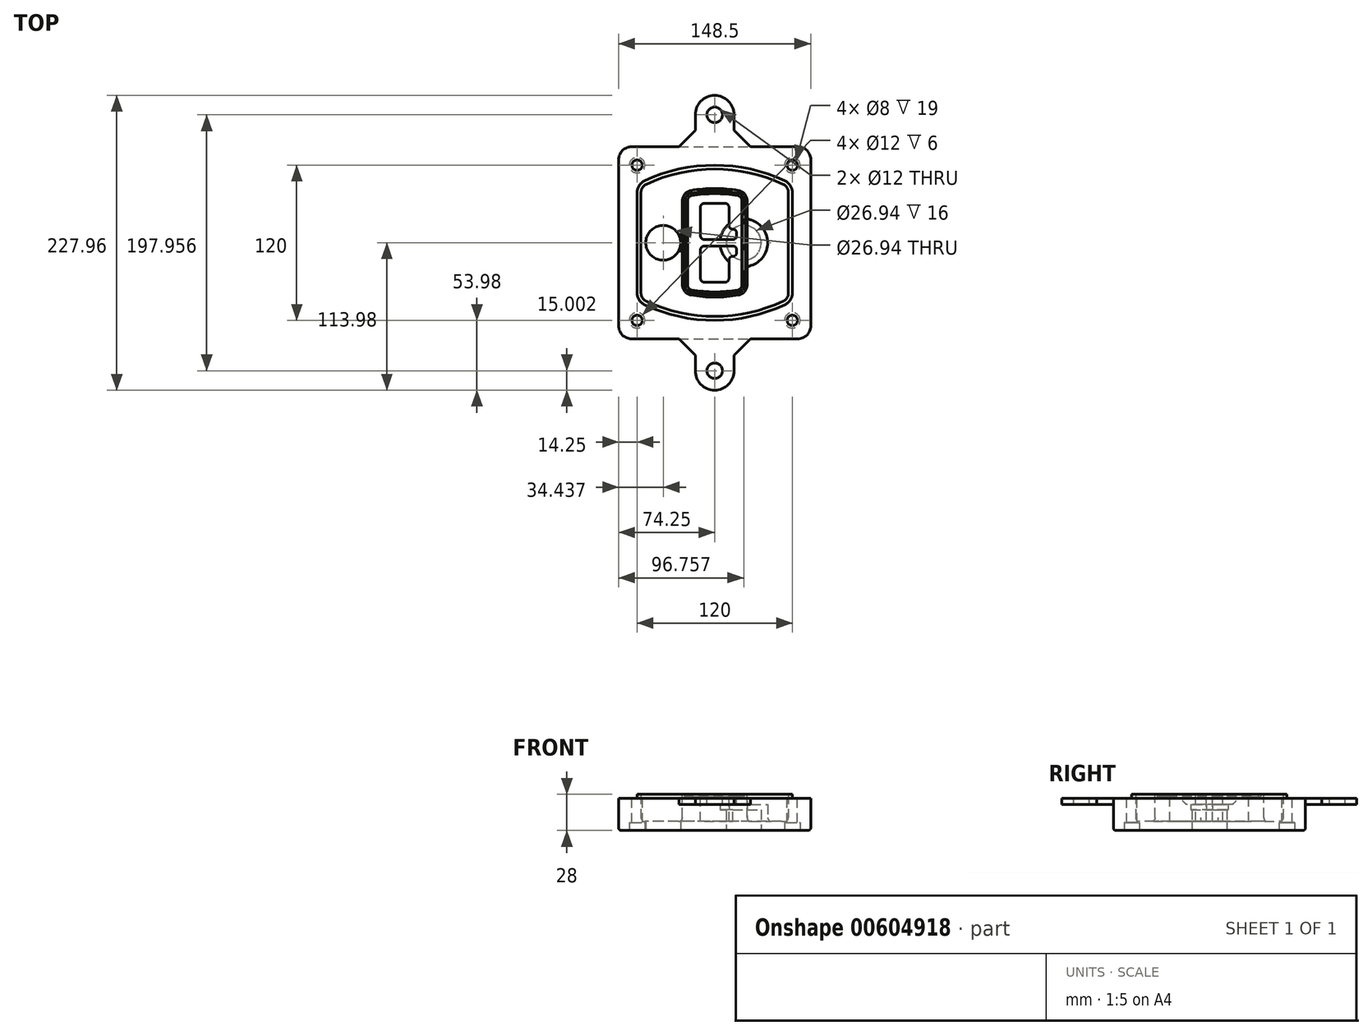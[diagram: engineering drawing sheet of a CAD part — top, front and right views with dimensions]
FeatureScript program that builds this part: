
annotation { "Feature Type Name" : "Feature", "Feature Type Description" : "" }
export const myFeature = defineFeature(function(context is Context, id is Id, definition is map)
    precondition{}
    {
        {
            var Q0;
            Q0=qCreatedBy(makeId("Top.planeOp"),FACE);
            var sketch = newSketch(context, id + "F0", { "sketchPlane" : qUnion([Q0])});
            skPoint(sketch, "E0.rect.middle", {"position": v(0, 0) * mm});
            skLineSegment(sketch, "E1.bottom", {"start": v(-64.25, -74.25) * mm, "end": v(64.25, -74.25) * mm});
            skLineSegment(sketch, "E1.top", {"start": v(-64.25, 74.25) * mm, "end": v(64.25, 74.25) * mm});
            skLineSegment(sketch, "E1.left", {"start": v(-74.25, -64.25) * mm, "end": v(-74.25, 64.25) * mm});
            skLineSegment(sketch, "E1.right", {"start": v(74.25, -64.25) * mm, "end": v(74.25, 64.25) * mm});
            skLineSegment(sketch, "E2", {"start": v(-74.25, 74.25) * mm, "end": v(74.25, -74.25) * mm, "construction": true});
            skLineSegment(sketch, "E3", {"start": v(74.25, 74.25) * mm, "end": v(-74.25, -74.25) * mm, "construction": true});
            skCircle(sketch, "E4", {"center": v(-60, 60) * mm, "radius": 4 * mm});
            skCircle(sketch, "E5", {"center": v(60, 60) * mm, "radius": 4 * mm});
            skCircle(sketch, "E6", {"center": v(60, -60) * mm, "radius": 4 * mm});
            skCircle(sketch, "E7", {"center": v(-60, -60) * mm, "radius": 4 * mm});
            skLineSegment(sketch, "E8", {"start": v(-60, 60) * mm, "end": v(60, 60) * mm, "construction": true});
            skLineSegment(sketch, "E9", {"start": v(60, 60) * mm, "end": v(60, -60) * mm, "construction": true});
            skLineSegment(sketch, "E10", {"start": v(60, -60) * mm, "end": v(-60, -60) * mm, "construction": true});
            skLineSegment(sketch, "E11", {"start": v(-60, -60) * mm, "end": v(-60, 60) * mm, "construction": true});
            skLineSegment(sketch, "E12", {"start": v(-60, 38.83) * mm, "end": v(-60, -38.83) * mm});
            skLineSegment(sketch, "E13", {"start": v(60, 38.83) * mm, "end": v(60, -38.83) * mm});
            skArc(sketch, "E14", {"start": v(54.26, 47.88) * mm, "mid": v(0, 60) * mm, "end": v(-54.26, 47.88) * mm});
            skArc(sketch, "E15", {"start": v(-54.26, -47.88) * mm, "mid": v(0, -60) * mm, "end": v(54.26, -47.88) * mm});
            skLineSegment(sketch, "E16", {"start": v(-60, 0) * mm, "end": v(60, 0) * mm, "construction": true});
            skPoint(sketch, "E17.visualSharp", {"position": v(-60, -45) * mm});
            skArc(sketch, "E17.filletArc", {"start": v(-60, -38.83) * mm, "mid": v(-58.44, -44.2) * mm, "end": v(-54.26, -47.88) * mm});
            skPoint(sketch, "E18.visualSharp", {"position": v(-60, 45) * mm});
            skArc(sketch, "E18.filletArc", {"start": v(-54.26, 47.88) * mm, "mid": v(-58.44, 44.2) * mm, "end": v(-60, 38.83) * mm});
            skPoint(sketch, "E19.visualSharp", {"position": v(60, 45) * mm});
            skArc(sketch, "E19.filletArc", {"start": v(60, 38.83) * mm, "mid": v(58.44, 44.2) * mm, "end": v(54.26, 47.88) * mm});
            skPoint(sketch, "E20.visualSharp", {"position": v(60, -45) * mm});
            skArc(sketch, "E20.filletArc", {"start": v(54.26, -47.88) * mm, "mid": v(58.44, -44.2) * mm, "end": v(60, -38.83) * mm});
            skPoint(sketch, "E21.visualSharp", {"position": v(-74.25, 74.25) * mm});
            skArc(sketch, "E21.filletArc", {"start": v(-64.25, 74.25) * mm, "mid": v(-71.32, 71.32) * mm, "end": v(-74.25, 64.25) * mm});
            skPoint(sketch, "E22.visualSharp", {"position": v(74.25, 74.25) * mm});
            skArc(sketch, "E22.filletArc", {"start": v(74.25, 64.25) * mm, "mid": v(71.32, 71.32) * mm, "end": v(64.25, 74.25) * mm});
            skPoint(sketch, "E23.visualSharp", {"position": v(74.25, -74.25) * mm});
            skArc(sketch, "E23.filletArc", {"start": v(64.25, -74.25) * mm, "mid": v(71.32, -71.32) * mm, "end": v(74.25, -64.25) * mm});
            skPoint(sketch, "E24.visualSharp", {"position": v(-74.25, -74.25) * mm});
            skArc(sketch, "E24.filletArc", {"start": v(-74.25, -64.25) * mm, "mid": v(-71.32, -71.32) * mm, "end": v(-64.25, -74.25) * mm});
            skArc(sketch, "E25.0", {"start": v(57, 38.83) * mm, "mid": v(55.9, 42.58) * mm, "end": v(52.98, 45.17) * mm});
            skLineSegment(sketch, "E25.1", {"start": v(57, 38.83) * mm, "end": v(57, -38.83) * mm});
            skArc(sketch, "E25.2", {"start": v(52.98, -45.17) * mm, "mid": v(55.9, -42.58) * mm, "end": v(57, -38.83) * mm});
            skArc(sketch, "E25.3", {"start": v(-52.98, -45.17) * mm, "mid": v(0, -57) * mm, "end": v(52.98, -45.17) * mm});
            skArc(sketch, "E25.4", {"start": v(-57, -38.83) * mm, "mid": v(-55.9, -42.58) * mm, "end": v(-52.98, -45.17) * mm});
            skArc(sketch, "E25.5", {"start": v(52.98, 45.17) * mm, "mid": v(0, 57) * mm, "end": v(-52.98, 45.17) * mm});
            skLineSegment(sketch, "E25.6", {"start": v(-57, 38.83) * mm, "end": v(-57, -38.83) * mm});
            skArc(sketch, "E25.7", {"start": v(-52.98, 45.17) * mm, "mid": v(-55.9, 42.58) * mm, "end": v(-57, 38.83) * mm});
            skArc(sketch, "E26.0", {"start": v(-55.96, 51.5) * mm, "mid": v(-61.82, 46.33) * mm, "end": v(-64, 38.83) * mm});
            skArc(sketch, "E26.1", {"start": v(55.96, 51.5) * mm, "mid": v(0, 64) * mm, "end": v(-55.96, 51.5) * mm});
            skArc(sketch, "E26.2", {"start": v(64, 38.83) * mm, "mid": v(61.82, 46.33) * mm, "end": v(55.96, 51.5) * mm});
            skLineSegment(sketch, "E26.3", {"start": v(64, 38.83) * mm, "end": v(64, -38.83) * mm});
            skArc(sketch, "E26.4", {"start": v(55.96, -51.5) * mm, "mid": v(61.82, -46.33) * mm, "end": v(64, -38.83) * mm});
            skLineSegment(sketch, "E26.5", {"start": v(-64, 38.83) * mm, "end": v(-64, -38.83) * mm});
            skArc(sketch, "E26.6", {"start": v(-55.96, -51.5) * mm, "mid": v(0, -64) * mm, "end": v(55.96, -51.5) * mm});
            skArc(sketch, "E26.7", {"start": v(-64, -38.83) * mm, "mid": v(-61.82, -46.33) * mm, "end": v(-55.96, -51.5) * mm});
            skSolve(sketch);
        }
        {
            var Q0;
            Q0=makeQuery(id+"F0.imprint","IMPRINT",FACE,{"disambiguationData":[TD([[makeQuery(id+"F0.imprint","IMPRINT",EDGE,{"derivedFrom":sQuery(id+"F0.wireOp",EDGE,"E1.bottom")}),1.0]])]});
            var Q1;
            Q1=makeQuery(id+"F0.imprint","IMPRINT",FACE,{"disambiguationData":[TD([[makeQuery(id+"F0.imprint","IMPRINT",EDGE,{"derivedFrom":sQuery(id+"F0.wireOp",EDGE,"E12")}),1.0]])]});
            var Q2;
            Q2=makeQuery(id+"F0.imprint","IMPRINT",FACE,{"disambiguationData":[TD([[makeQuery(id+"F0.imprint","IMPRINT",EDGE,{"derivedFrom":sQuery(id+"F0.wireOp",EDGE,"E25.0")}),1.0]])]});
            var Q3;
            Q3=makeQuery(id+"F0.imprint","IMPRINT",FACE,{"disambiguationData":[TD([[makeQuery(id+"F0.imprint","IMPRINT",EDGE,{"derivedFrom":sQuery(id+"F0.wireOp",EDGE,"E12")}),-1.0]])]});
            extrude(context, id + "F1", {"entities" : qUnion([Q0, Q1, Q2, Q3]), "oppositeDirection" : true, "depth" : 25 * mm});
        }
        {
            var Q0;
            Q0=makeQuery(id+"F0.imprint","IMPRINT",FACE,{"disambiguationData":[TD([[makeQuery(id+"F0.imprint","IMPRINT",EDGE,{"derivedFrom":sQuery(id+"F0.wireOp",EDGE,"E12")}),1.0]])]});
            extrude(context, id + "F2", {"entities" : qUnion([Q0]), "operationType" : NewBodyOperationType.ADD, "depth" : 3 * mm});
        }
        {
            var Q0;
            Q0=makeQuery(id+"F0.imprint","IMPRINT",FACE,{"disambiguationData":[TD([[makeQuery(id+"F0.imprint","IMPRINT",EDGE,{"derivedFrom":sQuery(id+"F0.wireOp",EDGE,"E25.0")}),1.0]])]});
            extrude(context, id + "F3", {"entities" : qUnion([Q0]), "operationType" : NewBodyOperationType.REMOVE, "oppositeDirection" : true, "depth" : 18 * mm});
        }
        {
            var Q0;
            Q0=makeQuery(id+"F2.opExtrude","CAP_FACE",FACE,{"disambiguationData":[OSD([sQuery(id+"F0.wireOp",EDGE,"E12"),sQuery(id+"F0.wireOp",EDGE,"E13"),sQuery(id+"F0.wireOp",EDGE,"E14"),sQuery(id+"F0.wireOp",EDGE,"E15"),sQuery(id+"F0.wireOp",EDGE,"E17.filletArc"),sQuery(id+"F0.wireOp",EDGE,"E18.filletArc"),sQuery(id+"F0.wireOp",EDGE,"E19.filletArc"),sQuery(id+"F0.wireOp",EDGE,"E20.filletArc"),sQuery(id+"F0.wireOp",EDGE,"E25.0"),sQuery(id+"F0.wireOp",EDGE,"E25.1"),sQuery(id+"F0.wireOp",EDGE,"E25.2"),sQuery(id+"F0.wireOp",EDGE,"E25.3"),sQuery(id+"F0.wireOp",EDGE,"E25.4"),sQuery(id+"F0.wireOp",EDGE,"E25.5"),sQuery(id+"F0.wireOp",EDGE,"E25.6"),sQuery(id+"F0.wireOp",EDGE,"E25.7")])],"isStart":false});
            var sketch = newSketch(context, id + "F4", { "sketchPlane" : qUnion([Q0])});
            skArc(sketch, "E27.0", {"start": v(-18.34, -40.45) * mm, "mid": v(0, -42) * mm, "end": v(18.34, -40.45) * mm});
            skArc(sketch, "E28.0", {"start": v(18.34, 40.45) * mm, "mid": v(0, 42) * mm, "end": v(-18.34, 40.45) * mm});
            skLineSegment(sketch, "E29", {"start": v(-25, 32.57) * mm, "end": v(-25, -32.57) * mm});
            skLineSegment(sketch, "E30", {"start": v(25, 32.57) * mm, "end": v(25, -32.57) * mm});
            skLineSegment(sketch, "E31", {"start": v(-25, 39.1) * mm, "end": v(25, 39.1) * mm, "construction": true});
            skLineSegment(sketch, "E32", {"start": v(-25, -39.1) * mm, "end": v(25, -39.1) * mm, "construction": true});
            skPoint(sketch, "E33.visualSharp", {"position": v(-25, 39.1) * mm});
            skArc(sketch, "E33.filletArc", {"start": v(-18.34, 40.45) * mm, "mid": v(-23.11, 37.73) * mm, "end": v(-25, 32.57) * mm});
            skPoint(sketch, "E34.visualSharp", {"position": v(25, 39.1) * mm});
            skArc(sketch, "E34.filletArc", {"start": v(25, 32.57) * mm, "mid": v(23.11, 37.73) * mm, "end": v(18.34, 40.45) * mm});
            skPoint(sketch, "E35.visualSharp", {"position": v(25, -39.1) * mm});
            skArc(sketch, "E35.filletArc", {"start": v(18.34, -40.45) * mm, "mid": v(23.11, -37.73) * mm, "end": v(25, -32.57) * mm});
            skPoint(sketch, "E36.visualSharp", {"position": v(-25, -39.1) * mm});
            skArc(sketch, "E36.filletArc", {"start": v(-25, -32.57) * mm, "mid": v(-23.11, -37.73) * mm, "end": v(-18.34, -40.45) * mm});
            skArc(sketch, "E37.0", {"start": v(52.98, 45.17) * mm, "mid": v(0, 57) * mm, "end": v(-52.98, 45.17) * mm});
            skArc(sketch, "E37.1", {"start": v(-52.98, 45.17) * mm, "mid": v(-55.9, 42.58) * mm, "end": v(-57, 38.83) * mm});
            skLineSegment(sketch, "E37.2", {"start": v(-57, 38.83) * mm, "end": v(-57, -38.83) * mm});
            skArc(sketch, "E37.3", {"start": v(-57, -38.83) * mm, "mid": v(-55.9, -42.58) * mm, "end": v(-52.98, -45.17) * mm});
            skArc(sketch, "E37.4", {"start": v(-52.98, -45.17) * mm, "mid": v(0, -57) * mm, "end": v(52.98, -45.17) * mm});
            skArc(sketch, "E37.5", {"start": v(52.98, -45.17) * mm, "mid": v(55.9, -42.58) * mm, "end": v(57, -38.83) * mm});
            skLineSegment(sketch, "E37.6", {"start": v(57, 38.83) * mm, "end": v(57, -38.83) * mm});
            skArc(sketch, "E37.7", {"start": v(57, 38.83) * mm, "mid": v(55.9, 42.58) * mm, "end": v(52.98, 45.17) * mm});
            skLineSegment(sketch, "E38.0", {"start": v(23, 32.57) * mm, "end": v(23, -32.57) * mm});
            skArc(sketch, "E38.1", {"start": v(18, -38.48) * mm, "mid": v(21.58, -36.44) * mm, "end": v(23, -32.57) * mm});
            skArc(sketch, "E38.2", {"start": v(-18, -38.48) * mm, "mid": v(0, -40) * mm, "end": v(18, -38.48) * mm});
            skArc(sketch, "E38.3", {"start": v(-23, -32.57) * mm, "mid": v(-21.58, -36.44) * mm, "end": v(-18, -38.48) * mm});
            skLineSegment(sketch, "E38.4", {"start": v(-23, 32.57) * mm, "end": v(-23, -32.57) * mm});
            skArc(sketch, "E38.5", {"start": v(23, 32.57) * mm, "mid": v(21.58, 36.44) * mm, "end": v(18, 38.48) * mm});
            skArc(sketch, "E38.6", {"start": v(-18, 38.48) * mm, "mid": v(-21.58, 36.44) * mm, "end": v(-23, 32.57) * mm});
            skArc(sketch, "E38.7", {"start": v(18, 38.48) * mm, "mid": v(0, 40) * mm, "end": v(-18, 38.48) * mm});
            skArc(sketch, "E39.0", {"start": v(21, 32.57) * mm, "mid": v(20.06, 35.15) * mm, "end": v(17.67, 36.5) * mm});
            skLineSegment(sketch, "E39.1", {"start": v(21, 32.57) * mm, "end": v(21, -32.57) * mm});
            skArc(sketch, "E39.2", {"start": v(17.67, -36.5) * mm, "mid": v(20.06, -35.15) * mm, "end": v(21, -32.57) * mm});
            skArc(sketch, "E39.3", {"start": v(-17.67, -36.5) * mm, "mid": v(0, -38) * mm, "end": v(17.67, -36.5) * mm});
            skArc(sketch, "E39.4", {"start": v(-21, -32.57) * mm, "mid": v(-20.06, -35.15) * mm, "end": v(-17.67, -36.5) * mm});
            skArc(sketch, "E39.5", {"start": v(17.67, 36.5) * mm, "mid": v(0, 38) * mm, "end": v(-17.67, 36.5) * mm});
            skLineSegment(sketch, "E39.6", {"start": v(-21, 32.57) * mm, "end": v(-21, -32.57) * mm});
            skArc(sketch, "E39.7", {"start": v(-17.67, 36.5) * mm, "mid": v(-20.06, 35.15) * mm, "end": v(-21, 32.57) * mm});
            skLineSegment(sketch, "E40", {"start": v(-25, 0) * mm, "end": v(25, 0) * mm, "construction": true});
            skLineSegment(sketch, "E41", {"start": v(-11, 5.5) * mm, "end": v(-11, 27.5) * mm});
            skLineSegment(sketch, "E42", {"start": v(-8, 30.5) * mm, "end": v(8, 30.5) * mm});
            skLineSegment(sketch, "E43", {"start": v(11, 27.5) * mm, "end": v(11, 13.5) * mm});
            skLineSegment(sketch, "E44", {"start": v(14, 10.5) * mm, "end": v(14, 10.5) * mm});
            skLineSegment(sketch, "E45", {"start": v(17, 7.5) * mm, "end": v(17, 5.5) * mm});
            skLineSegment(sketch, "E46", {"start": v(14, 2.5) * mm, "end": v(-8, 2.5) * mm});
            skPoint(sketch, "E47.visualSharp", {"position": v(-11, 30.5) * mm});
            skArc(sketch, "E47.filletArc", {"start": v(-8, 30.5) * mm, "mid": v(-10.12, 29.62) * mm, "end": v(-11, 27.5) * mm});
            skPoint(sketch, "E48.visualSharp", {"position": v(11, 30.5) * mm});
            skArc(sketch, "E48.filletArc", {"start": v(11, 27.5) * mm, "mid": v(10.12, 29.62) * mm, "end": v(8, 30.5) * mm});
            skPoint(sketch, "E49.visualSharp", {"position": v(11, 10.5) * mm});
            skArc(sketch, "E49.filletArc", {"start": v(11, 13.5) * mm, "mid": v(11.88, 11.38) * mm, "end": v(14, 10.5) * mm});
            skPoint(sketch, "E50.visualSharp", {"position": v(17, 10.5) * mm});
            skArc(sketch, "E50.filletArc", {"start": v(17, 7.5) * mm, "mid": v(16.12, 9.62) * mm, "end": v(14, 10.5) * mm});
            skPoint(sketch, "E51.visualSharp", {"position": v(17, 2.5) * mm});
            skArc(sketch, "E51.filletArc", {"start": v(14, 2.5) * mm, "mid": v(16.12, 3.38) * mm, "end": v(17, 5.5) * mm});
            skPoint(sketch, "E52.visualSharp", {"position": v(-11, 2.5) * mm});
            skArc(sketch, "E52.filletArc", {"start": v(-11, 5.5) * mm, "mid": v(-10.12, 3.38) * mm, "end": v(-8, 2.5) * mm});
            skLineSegment(sketch, "E53.0.MirrorCS", {"start": v(14, -2.5) * mm, "end": v(-8, -2.5) * mm});
            skArc(sketch, "E54.0.MirrorCS", {"start": v(-11, -5.5) * mm, "mid": v(-10.12, -3.38) * mm, "end": v(-8, -2.5) * mm});
            skLineSegment(sketch, "E55.0.MirrorCS", {"start": v(-11, -5.5) * mm, "end": v(-11, -27.5) * mm});
            skArc(sketch, "E56.0.MirrorCS", {"start": v(-8, -30.5) * mm, "mid": v(-10.12, -29.62) * mm, "end": v(-11, -27.5) * mm});
            skLineSegment(sketch, "E57.0.MirrorCS", {"start": v(-8, -30.5) * mm, "end": v(8, -30.5) * mm});
            skArc(sketch, "E58.0.MirrorCS", {"start": v(11, -27.5) * mm, "mid": v(10.12, -29.62) * mm, "end": v(8, -30.5) * mm});
            skLineSegment(sketch, "E59.0.MirrorCS", {"start": v(11, -27.5) * mm, "end": v(11, -13.5) * mm});
            skArc(sketch, "E60.0.MirrorCS", {"start": v(11, -13.5) * mm, "mid": v(11.88, -11.38) * mm, "end": v(14, -10.5) * mm});
            skArc(sketch, "E61.0.MirrorCS", {"start": v(17, -7.5) * mm, "mid": v(16.12, -9.62) * mm, "end": v(14, -10.5) * mm});
            skLineSegment(sketch, "E62.0.MirrorCS", {"start": v(17, -7.5) * mm, "end": v(17, -5.5) * mm});
            skArc(sketch, "E63.0.MirrorCS", {"start": v(14, -2.5) * mm, "mid": v(16.12, -3.38) * mm, "end": v(17, -5.5) * mm});
            skSolve(sketch);
        }
        {
            var Q0;
            Q0=makeQuery(id+"F4.imprint","IMPRINT",FACE,{"disambiguationData":[TD([[makeQuery(id+"F4.imprint","IMPRINT",EDGE,{"derivedFrom":sQuery(id+"F4.wireOp",EDGE,"E27.0")}),1.0]])]});
            var Q1;
            Q1=makeQuery(id+"F4.imprint","IMPRINT",FACE,{"disambiguationData":[TD([[makeQuery(id+"F4.imprint","IMPRINT",EDGE,{"derivedFrom":sQuery(id+"F4.wireOp",EDGE,"E38.0")}),-1.0]])]});
            var Q2;
            Q2=makeQuery(id+"F4.imprint","IMPRINT",FACE,{"disambiguationData":[TD([[makeQuery(id+"F4.imprint","IMPRINT",EDGE,{"derivedFrom":sQuery(id+"F4.wireOp",EDGE,"E39.0")}),1.0]])]});
            extrude(context, id + "F5", {"entities" : qUnion([Q0, Q1, Q2]), "operationType" : NewBodyOperationType.ADD, "endBound" : BoundingType.UP_TO_NEXT, "oppositeDirection" : true, "depth" : 25 * mm});
        }
        {
            var Q0;
            Q0=makeQuery(id+"F4.imprint","IMPRINT",FACE,{"disambiguationData":[TD([[makeQuery(id+"F4.imprint","IMPRINT",EDGE,{"derivedFrom":sQuery(id+"F4.wireOp",EDGE,"E38.0")}),-1.0]])]});
            extrude(context, id + "F6", {"entities" : qUnion([Q0]), "operationType" : NewBodyOperationType.REMOVE, "oppositeDirection" : true, "depth" : 2 * mm});
        }
        {
            var Q0;
            Q0=makeQuery(id+"F1.opExtrude","CAP_FACE",FACE,{"disambiguationData":[OSD([sQuery(id+"F0.wireOp",EDGE,"E1.bottom"),sQuery(id+"F0.wireOp",EDGE,"E1.top"),sQuery(id+"F0.wireOp",EDGE,"E1.left"),sQuery(id+"F0.wireOp",EDGE,"E1.right"),sQuery(id+"F0.wireOp",EDGE,"E4"),sQuery(id+"F0.wireOp",EDGE,"E5"),sQuery(id+"F0.wireOp",EDGE,"E6"),sQuery(id+"F0.wireOp",EDGE,"E7"),sQuery(id+"F0.wireOp",EDGE,"E21.filletArc"),sQuery(id+"F0.wireOp",EDGE,"E22.filletArc"),sQuery(id+"F0.wireOp",EDGE,"E23.filletArc"),sQuery(id+"F0.wireOp",EDGE,"E24.filletArc")])],"isStart":false});
            var sketch = newSketch(context, id + "F7", { "sketchPlane" : qUnion([Q0])});
            skCircle(sketch, "E64", {"center": v(22.5, 0) * mm, "radius": 13.47 * mm});
            skCircle(sketch, "E65", {"center": v(-39.81, 0) * mm, "radius": 13.47 * mm});
            skLineSegment(sketch, "E66", {"start": v(74.25, 0) * mm, "end": v(-74.25, 0) * mm});
            skCircle(sketch, "E67", {"center": v(22.5, 0) * mm, "radius": 18.47 * mm});
            skCircle(sketch, "E68", {"center": v(60, -60) * mm, "radius": 6 * mm});
            skCircle(sketch, "E69", {"center": v(-60, -60) * mm, "radius": 6 * mm});
            skCircle(sketch, "E70", {"center": v(-60, 60) * mm, "radius": 6 * mm});
            skCircle(sketch, "E71", {"center": v(60, 60) * mm, "radius": 6 * mm});
            skSolve(sketch);
        }
        {
            var Q0;
            {var subQ1=sQuery(id+"F7.wireOp",EDGE,"E66");var subQ4=sQuery(id+"F7.wireOp",EDGE,"E64");var subQ6=makeQuery(id+"F7.imprint","INTERSECT",VERTEX,{"disambiguationData":[OD(0.0)],"derivedFrom":[subQ4,subQ1]});Q0=makeQuery(id+"F7.imprint","IMPRINT",FACE,{"disambiguationData":[TD([[makeQuery(id+"F7.imprint","IMPRINT",EDGE,{"disambiguationData":[TD([[subQ6,-1.0]])],"derivedFrom":subQ4}),-1.0]])]});}
            var Q1;
            {var subQ0=sQuery(id+"F7.wireOp",EDGE,"E66");var subQ1=sQuery(id+"F7.wireOp",EDGE,"E64");var subQ3=makeQuery(id+"F7.imprint","INTERSECT",VERTEX,{"disambiguationData":[OD(0.0)],"derivedFrom":[subQ1,subQ0]});Q1=makeQuery(id+"F7.imprint","IMPRINT",FACE,{"disambiguationData":[TD([[makeQuery(id+"F7.imprint","IMPRINT",EDGE,{"disambiguationData":[TD([[subQ3,-1.0]])],"derivedFrom":subQ1}),1.0]])]});}
            var Q2;
            {var subQ0=sQuery(id+"F7.wireOp",EDGE,"E66");var subQ1=sQuery(id+"F7.wireOp",EDGE,"E64");var subQ3=makeQuery(id+"F7.imprint","INTERSECT",VERTEX,{"disambiguationData":[OD(0.0)],"derivedFrom":[subQ1,subQ0]});Q2=makeQuery(id+"F7.imprint","IMPRINT",FACE,{"disambiguationData":[TD([[makeQuery(id+"F7.imprint","IMPRINT",EDGE,{"disambiguationData":[TD([[subQ3,1.0]])],"derivedFrom":subQ1}),1.0]])]});}
            var Q3;
            {var subQ1=sQuery(id+"F7.wireOp",EDGE,"E66");var subQ4=sQuery(id+"F7.wireOp",EDGE,"E64");var subQ6=makeQuery(id+"F7.imprint","INTERSECT",VERTEX,{"disambiguationData":[OD(0.0)],"derivedFrom":[subQ4,subQ1]});Q3=makeQuery(id+"F7.imprint","IMPRINT",FACE,{"disambiguationData":[TD([[makeQuery(id+"F7.imprint","IMPRINT",EDGE,{"disambiguationData":[TD([[subQ6,1.0]])],"derivedFrom":subQ4}),-1.0]])]});}
            extrude(context, id + "F8", {"entities" : qUnion([Q0, Q1, Q2, Q3]), "operationType" : NewBodyOperationType.ADD, "oppositeDirection" : true, "depth" : 20 * mm});
        }
        {
            var Q0;
            {var subQ0=sQuery(id+"F7.wireOp",EDGE,"E66");var subQ1=sQuery(id+"F7.wireOp",EDGE,"E64");var subQ3=makeQuery(id+"F7.imprint","INTERSECT",VERTEX,{"disambiguationData":[OD(0.0)],"derivedFrom":[subQ1,subQ0]});Q0=makeQuery(id+"F7.imprint","IMPRINT",FACE,{"disambiguationData":[TD([[makeQuery(id+"F7.imprint","IMPRINT",EDGE,{"disambiguationData":[TD([[subQ3,-1.0]])],"derivedFrom":subQ1}),1.0]])]});}
            var Q1;
            {var subQ0=sQuery(id+"F7.wireOp",EDGE,"E66");var subQ1=sQuery(id+"F7.wireOp",EDGE,"E64");var subQ3=makeQuery(id+"F7.imprint","INTERSECT",VERTEX,{"disambiguationData":[OD(0.0)],"derivedFrom":[subQ1,subQ0]});Q1=makeQuery(id+"F7.imprint","IMPRINT",FACE,{"disambiguationData":[TD([[makeQuery(id+"F7.imprint","IMPRINT",EDGE,{"disambiguationData":[TD([[subQ3,1.0]])],"derivedFrom":subQ1}),1.0]])]});}
            extrude(context, id + "F9", {"entities" : qUnion([Q0, Q1]), "operationType" : NewBodyOperationType.REMOVE, "oppositeDirection" : true, "depth" : 16 * mm});
        }
        {
            var Q0;
            {var subQ0=sQuery(id+"F7.wireOp",EDGE,"E66");var subQ1=sQuery(id+"F7.wireOp",EDGE,"E65");var subQ3=makeQuery(id+"F7.imprint","INTERSECT",VERTEX,{"disambiguationData":[OD(0.0)],"derivedFrom":[subQ1,subQ0]});Q0=makeQuery(id+"F7.imprint","IMPRINT",FACE,{"disambiguationData":[TD([[makeQuery(id+"F7.imprint","IMPRINT",EDGE,{"disambiguationData":[TD([[subQ3,-1.0]])],"derivedFrom":subQ1}),1.0]])]});}
            var Q1;
            {var subQ0=sQuery(id+"F7.wireOp",EDGE,"E66");var subQ1=sQuery(id+"F7.wireOp",EDGE,"E65");var subQ3=makeQuery(id+"F7.imprint","INTERSECT",VERTEX,{"disambiguationData":[OD(0.0)],"derivedFrom":[subQ1,subQ0]});Q1=makeQuery(id+"F7.imprint","IMPRINT",FACE,{"disambiguationData":[TD([[makeQuery(id+"F7.imprint","IMPRINT",EDGE,{"disambiguationData":[TD([[subQ3,1.0]])],"derivedFrom":subQ1}),1.0]])]});}
            extrude(context, id + "F10", {"entities" : qUnion([Q0, Q1]), "operationType" : NewBodyOperationType.REMOVE, "oppositeDirection" : true, "depth" : 25 * mm});
        }
        {
            var Q0;
            Q0=makeQuery(id+"F7.imprint","IMPRINT",FACE,{"disambiguationData":[TD([[makeQuery(id+"F7.imprint","IMPRINT",EDGE,{"derivedFrom":sQuery(id+"F7.wireOp",EDGE,"E68")}),1.0]])]});
            var Q1;
            Q1=makeQuery(id+"F7.imprint","IMPRINT",FACE,{"disambiguationData":[TD([[makeQuery(id+"F7.imprint","IMPRINT",EDGE,{"derivedFrom":makeQuery(id+"F1.opExtrude","CAP_EDGE",EDGE,{"disambiguationData":[OSD([sQuery(id+"F0.wireOp",EDGE,"E5")])],"isStart":false})}),-1.0]])]});
            var Q2;
            Q2=makeQuery(id+"F7.imprint","IMPRINT",FACE,{"disambiguationData":[TD([[makeQuery(id+"F7.imprint","IMPRINT",EDGE,{"derivedFrom":sQuery(id+"F7.wireOp",EDGE,"E69")}),1.0]])]});
            var Q3;
            Q3=makeQuery(id+"F7.imprint","IMPRINT",FACE,{"disambiguationData":[TD([[makeQuery(id+"F7.imprint","IMPRINT",EDGE,{"derivedFrom":makeQuery(id+"F1.opExtrude","CAP_EDGE",EDGE,{"disambiguationData":[OSD([sQuery(id+"F0.wireOp",EDGE,"E4")])],"isStart":false})}),-1.0]])]});
            var Q4;
            Q4=makeQuery(id+"F7.imprint","IMPRINT",FACE,{"disambiguationData":[TD([[makeQuery(id+"F7.imprint","IMPRINT",EDGE,{"derivedFrom":sQuery(id+"F7.wireOp",EDGE,"E70")}),1.0]])]});
            var Q5;
            Q5=makeQuery(id+"F7.imprint","IMPRINT",FACE,{"disambiguationData":[TD([[makeQuery(id+"F7.imprint","IMPRINT",EDGE,{"derivedFrom":makeQuery(id+"F1.opExtrude","CAP_EDGE",EDGE,{"disambiguationData":[OSD([sQuery(id+"F0.wireOp",EDGE,"E7")])],"isStart":false})}),-1.0]])]});
            var Q6;
            Q6=makeQuery(id+"F7.imprint","IMPRINT",FACE,{"disambiguationData":[TD([[makeQuery(id+"F7.imprint","IMPRINT",EDGE,{"derivedFrom":sQuery(id+"F7.wireOp",EDGE,"E71")}),1.0]])]});
            var Q7;
            Q7=makeQuery(id+"F7.imprint","IMPRINT",FACE,{"disambiguationData":[TD([[makeQuery(id+"F7.imprint","IMPRINT",EDGE,{"derivedFrom":makeQuery(id+"F1.opExtrude","CAP_EDGE",EDGE,{"disambiguationData":[OSD([sQuery(id+"F0.wireOp",EDGE,"E6")])],"isStart":false})}),-1.0]])]});
            extrude(context, id + "F11", {"entities" : qUnion([Q0, Q1, Q2, Q3, Q4, Q5, Q6, Q7]), "operationType" : NewBodyOperationType.REMOVE, "oppositeDirection" : true, "depth" : 6 * mm});
        }
        {
            var Q0;
            Q0=makeQuery(id+"F9.boolean.opBoolean","COPY",FACE,{"derivedFrom":makeQuery(id+"F9.opExtrude","CAP_FACE",FACE,{"disambiguationData":[OSD([sQuery(id+"F7.wireOp",EDGE,"E64")])],"isStart":false})});
            var sketch = newSketch(context, id + "F12", { "sketchPlane" : qUnion([Q0])});
            skArc(sketch, "E72.0", {"start": v(11, 14.45) * mm, "mid": v(6.45, 9.13) * mm, "end": v(4.2, 2.5) * mm});
            skArc(sketch, "E72.1", {"start": v(4.2, -2.5) * mm, "mid": v(6.45, -9.13) * mm, "end": v(11, -14.45) * mm});
            skLineSegment(sketch, "E73", {"start": v(4.2, -2.5) * mm, "end": v(14, -2.5) * mm});
            skLineSegment(sketch, "E74.0", {"start": v(14, 2.5) * mm, "end": v(4.2, 2.5) * mm});
            skArc(sketch, "E74.1", {"start": v(14, 2.5) * mm, "mid": v(16.12, 3.38) * mm, "end": v(17, 5.5) * mm});
            skLineSegment(sketch, "E74.2", {"start": v(17, 7.5) * mm, "end": v(17, 5.5) * mm});
            skArc(sketch, "E74.3", {"start": v(17, 7.5) * mm, "mid": v(16.12, 9.62) * mm, "end": v(14, 10.5) * mm});
            skArc(sketch, "E74.4", {"start": v(11, 13.5) * mm, "mid": v(11.88, 11.38) * mm, "end": v(14, 10.5) * mm});
            skLineSegment(sketch, "E74.5", {"start": v(11, 14.45) * mm, "end": v(11, 13.5) * mm});
            skLineSegment(sketch, "E74.7", {"start": v(14, -2.5) * mm, "end": v(4.2, -2.5) * mm});
            skArc(sketch, "E74.8", {"start": v(14, -2.5) * mm, "mid": v(16.12, -3.38) * mm, "end": v(17, -5.5) * mm});
            skLineSegment(sketch, "E74.9", {"start": v(17, -7.5) * mm, "end": v(17, -5.5) * mm});
            skArc(sketch, "E74.10", {"start": v(17, -7.5) * mm, "mid": v(16.12, -9.62) * mm, "end": v(14, -10.5) * mm});
            skArc(sketch, "E74.11", {"start": v(11, -13.5) * mm, "mid": v(11.88, -11.38) * mm, "end": v(14, -10.5) * mm});
            skLineSegment(sketch, "E74.12", {"start": v(11, -14.45) * mm, "end": v(11, -13.5) * mm});
            skPoint(sketch, "E75.orphan", {"position": v(11, -27.5) * mm});
            skPoint(sketch, "E76.orphan", {"position": v(-8, -2.5) * mm});
            skPoint(sketch, "E77.orphan", {"position": v(-8, 2.5) * mm});
            skPoint(sketch, "E78.orphan", {"position": v(11, 27.5) * mm});
            skSolve(sketch);
        }
        {
            var Q0;
            {var subQ7=sQuery(id+"F12.wireOp",EDGE,"E72.0");var subQ14=sQuery(id+"F12.wireOp",EDGE,"E72.1");var subQ16=sQuery(id+"F12.wireOp",EDGE,"E74.1");var subQ18=sQuery(id+"F12.wireOp",EDGE,"E74.8");Q0=qUnion([makeQuery(id+"F12.imprint","IMPRINT",FACE,{"disambiguationData":[TD([[makeQuery(id+"F12.imprint","IMPRINT",EDGE,{"derivedFrom":subQ7}),1.0]])]}),makeQuery(id+"F12.imprint","IMPRINT",FACE,{"disambiguationData":[TD([[makeQuery(id+"F12.imprint","IMPRINT",EDGE,{"derivedFrom":subQ14}),1.0]])]}),makeQuery(id+"F12.imprint","IMPRINT",FACE,{"disambiguationData":[TD([[makeQuery(id+"F12.imprint","IMPRINT",EDGE,{"derivedFrom":subQ16}),1.0]])]}),makeQuery(id+"F12.imprint","IMPRINT",FACE,{"disambiguationData":[TD([[makeQuery(id+"F12.imprint","IMPRINT",EDGE,{"derivedFrom":subQ18}),-1.0]])]})]);}
            var Q1;
            Q1=makeQuery(id+"F5.boolean.opBoolean","SPLIT",FACE,{"disambiguationData":[TD([makeQuery(id+"F5.opExtrude","SWEPT_FACE",FACE,{"disambiguationData":[OSD([sQuery(id+"F4.wireOp",EDGE,"E41")])]})])],"derivedFrom":makeQuery(id+"F3.boolean.opBoolean","COPY",FACE,{"derivedFrom":makeQuery(id+"F3.opExtrude","CAP_FACE",FACE,{"disambiguationData":[OSD([sQuery(id+"F0.wireOp",EDGE,"E25.0"),sQuery(id+"F0.wireOp",EDGE,"E25.1"),sQuery(id+"F0.wireOp",EDGE,"E25.2"),sQuery(id+"F0.wireOp",EDGE,"E25.3"),sQuery(id+"F0.wireOp",EDGE,"E25.4"),sQuery(id+"F0.wireOp",EDGE,"E25.5"),sQuery(id+"F0.wireOp",EDGE,"E25.6"),sQuery(id+"F0.wireOp",EDGE,"E25.7")])],"isStart":false})})});
            extrude(context, id + "F13", {"entities" : qUnion([Q0]), "operationType" : NewBodyOperationType.REMOVE, "endBound" : BoundingType.UP_TO_SURFACE, "endBoundEntityFace" : qUnion([Q1]), "depth" : 25 * mm});
        }
        {
            var Q0;
            Q0=makeQuery(id+"F3.boolean.opBoolean","COPY",EDGE,{"derivedFrom":makeQuery(id+"F3.opExtrude","CAP_EDGE",EDGE,{"disambiguationData":[OSD([sQuery(id+"F0.wireOp",EDGE,"E25.6")])],"isStart":false})});
            var Q1;
            Q1=makeQuery(id+"F8.boolean.opBoolean","INTERSECT",EDGE,{"derivedFrom":[makeQuery(id+"F5.opExtrude","SWEPT_FACE",FACE,{"disambiguationData":[OSD([sQuery(id+"F4.wireOp",EDGE,"E30")])]}),makeQuery(id+"F8.opExtrude","CAP_FACE",FACE,{"disambiguationData":[OSD([sQuery(id+"F7.wireOp",EDGE,"E67")])],"isStart":false})]});
            var Q2;
            Q2=makeQuery(id+"F8.boolean.opBoolean","INTERSECT",EDGE,{"disambiguationData":[OD(1.0)],"derivedFrom":[makeQuery(id+"F5.opExtrude","SWEPT_FACE",FACE,{"disambiguationData":[OSD([sQuery(id+"F4.wireOp",EDGE,"E30")])]}),makeQuery(id+"F8.opExtrude","SWEPT_FACE",FACE,{"disambiguationData":[OSD([sQuery(id+"F7.wireOp",EDGE,"E67")])]})]});
            var Q3;
            {var subQ0=sQuery(id+"F4.wireOp",EDGE,"E30");Q3=makeQuery(id+"F8.boolean.opBoolean","SPLIT",EDGE,{"disambiguationData":[TD([makeQuery(id+"F5.opExtrude","SWEPT_FACE",FACE,{"disambiguationData":[OSD([sQuery(id+"F4.wireOp",EDGE,"E35.filletArc")])]})])],"derivedFrom":makeQuery(id+"F5.opExtrude","CAP_EDGE",EDGE,{"disambiguationData":[OSD([subQ0])],"isStart":false})});}
            var Q4;
            {var subQ0=sQuery(id+"F0.wireOp",EDGE,"E25.7");var subQ1=sQuery(id+"F0.wireOp",EDGE,"E25.1");var subQ2=sQuery(id+"F0.wireOp",EDGE,"E25.6");var subQ3=sQuery(id+"F0.wireOp",EDGE,"E25.5");var subQ4=sQuery(id+"F0.wireOp",EDGE,"E25.4");var subQ5=sQuery(id+"F0.wireOp",EDGE,"E25.0");var subQ6=sQuery(id+"F0.wireOp",EDGE,"E25.2");var subQ7=sQuery(id+"F0.wireOp",EDGE,"E25.3");Q4=makeQuery(id+"F8.boolean.opBoolean","INTERSECT",EDGE,{"derivedFrom":[makeQuery(id+"F5.boolean.opBoolean","SPLIT",FACE,{"disambiguationData":[TD([makeQuery(id+"F2.opExtrude","SWEPT_FACE",FACE,{"disambiguationData":[OSD([subQ5])]})])],"derivedFrom":makeQuery(id+"F3.boolean.opBoolean","COPY",FACE,{"derivedFrom":makeQuery(id+"F3.opExtrude","CAP_FACE",FACE,{"disambiguationData":[OSD([subQ5,subQ1,subQ6,subQ7,subQ4,subQ3,subQ2,subQ0])],"isStart":false})})}),makeQuery(id+"F8.opExtrude","SWEPT_FACE",FACE,{"disambiguationData":[OSD([sQuery(id+"F7.wireOp",EDGE,"E67")])]})]});}
            var Q5;
            Q5=makeQuery(id+"F8.boolean.opBoolean","INTERSECT",EDGE,{"disambiguationData":[OD(0.0)],"derivedFrom":[makeQuery(id+"F5.opExtrude","SWEPT_FACE",FACE,{"disambiguationData":[OSD([sQuery(id+"F4.wireOp",EDGE,"E30")])]}),makeQuery(id+"F8.opExtrude","SWEPT_FACE",FACE,{"disambiguationData":[OSD([sQuery(id+"F7.wireOp",EDGE,"E67")])]})]});
            fillet(context, id + "F14", {"entities" : qUnion([Q0, Q1, Q2, Q3, Q4, Q5]), "radius" : 3 * mm, "tangentPropagation" : true, "allowEdgeOverflow" : false});
        }
        {
            var Q0;
            Q0=makeQuery(id+"F1.opExtrude","CAP_EDGE",EDGE,{"disambiguationData":[OSD([sQuery(id+"F0.wireOp",EDGE,"E1.bottom")])],"isStart":false});
            fillet(context, id + "F15", {"entities" : qUnion([Q0]), "radius" : 2 * mm, "tangentPropagation" : true, "allowEdgeOverflow" : false});
        }
        {
            var Q0;
            {var subQ0=sQuery(id+"F0.wireOp",EDGE,"E21.filletArc");var subQ1=sQuery(id+"F0.wireOp",EDGE,"E7");var subQ2=sQuery(id+"F0.wireOp",EDGE,"E6");var subQ3=sQuery(id+"F0.wireOp",EDGE,"E5");var subQ4=sQuery(id+"F0.wireOp",EDGE,"E4");var subQ5=sQuery(id+"F0.wireOp",EDGE,"E22.filletArc");var subQ6=sQuery(id+"F0.wireOp",EDGE,"E1.bottom");var subQ7=sQuery(id+"F0.wireOp",EDGE,"E1.right");var subQ8=sQuery(id+"F0.wireOp",EDGE,"E1.top");var subQ9=sQuery(id+"F0.wireOp",EDGE,"E1.left");var subQ10=sQuery(id+"F0.wireOp",EDGE,"E23.filletArc");var subQ11=sQuery(id+"F0.wireOp",EDGE,"E24.filletArc");Q0=makeQuery(id+"F2.boolean.opBoolean","SPLIT",FACE,{"disambiguationData":[TD([makeQuery(id+"F1.opExtrude","SWEPT_FACE",FACE,{"disambiguationData":[OSD([subQ6])]})])],"derivedFrom":makeQuery(id+"F1.opExtrude","CAP_FACE",FACE,{"disambiguationData":[OSD([subQ6,subQ8,subQ9,subQ7,subQ4,subQ3,subQ2,subQ1,subQ0,subQ5,subQ10,subQ11])],"isStart":true})});}
            var sketch = newSketch(context, id + "F16", { "sketchPlane" : qUnion([Q0])});
            skLineSegment(sketch, "E79", {"start": v(-27.73, 74.25) * mm, "end": v(-15, 86.98) * mm});
            skLineSegment(sketch, "E80", {"start": v(27.73, 74.25) * mm, "end": v(15, 86.98) * mm});
            skLineSegment(sketch, "E81", {"start": v(-15, 86.98) * mm, "end": v(-15, 98.98) * mm});
            skLineSegment(sketch, "E82", {"start": v(15, 86.98) * mm, "end": v(15, 98.98) * mm});
            skArc(sketch, "E83", {"start": v(0, 113.98) * mm, "mid": v(-10.6, 109.58) * mm, "end": v(-15, 98.98) * mm});
            skArc(sketch, "E84", {"start": v(15, 98.98) * mm, "mid": v(10.6, 109.58) * mm, "end": v(0, 113.98) * mm});
            skCircle(sketch, "E85", {"center": v(0, 98.98) * mm, "radius": 6 * mm});
            skLineSegment(sketch, "E86", {"start": v(-74.25, 0) * mm, "end": v(74.25, 0) * mm, "construction": true});
            skLineSegment(sketch, "E87.MirrorCS", {"start": v(-15, -86.98) * mm, "end": v(-15, -98.98) * mm});
            skLineSegment(sketch, "E88.MirrorCS", {"start": v(27.73, -74.25) * mm, "end": v(15, -86.98) * mm});
            skLineSegment(sketch, "E89.MirrorCS", {"start": v(15, -86.98) * mm, "end": v(15, -98.98) * mm});
            skArc(sketch, "E90.MirrorCS", {"start": v(15, -98.98) * mm, "mid": v(10.6, -109.58) * mm, "end": v(0, -113.98) * mm});
            skArc(sketch, "E91.MirrorCS", {"start": v(0, -113.98) * mm, "mid": v(-10.6, -109.58) * mm, "end": v(-15, -98.98) * mm});
            skLineSegment(sketch, "E92.MirrorCS", {"start": v(-27.73, -74.25) * mm, "end": v(-15, -86.98) * mm});
            skCircle(sketch, "E93.MirrorC", {"center": v(0, -98.98) * mm, "radius": 6 * mm});
            skSolve(sketch);
        }
        {
            var Q0;
            {var subQ1=sQuery(id+"F16.wireOp",EDGE,"E79");Q0=makeQuery(id+"F16.imprint","IMPRINT",FACE,{"disambiguationData":[TD([[makeQuery(id+"F16.imprint","IMPRINT",EDGE,{"derivedFrom":subQ1}),-1.0]])]});}
            var Q1;
            {var subQ0=sQuery(id+"F16.wireOp",EDGE,"E88.MirrorCS");Q1=makeQuery(id+"F16.imprint","IMPRINT",FACE,{"disambiguationData":[TD([[makeQuery(id+"F16.imprint","IMPRINT",EDGE,{"derivedFrom":subQ0}),-1.0]])]});}
            extrude(context, id + "F17", {"entities" : qUnion([Q0, Q1]), "operationType" : NewBodyOperationType.ADD, "oppositeDirection" : true, "depth" : 5 * mm, "offsetDistance" : 25 * mm});
        }
    });
